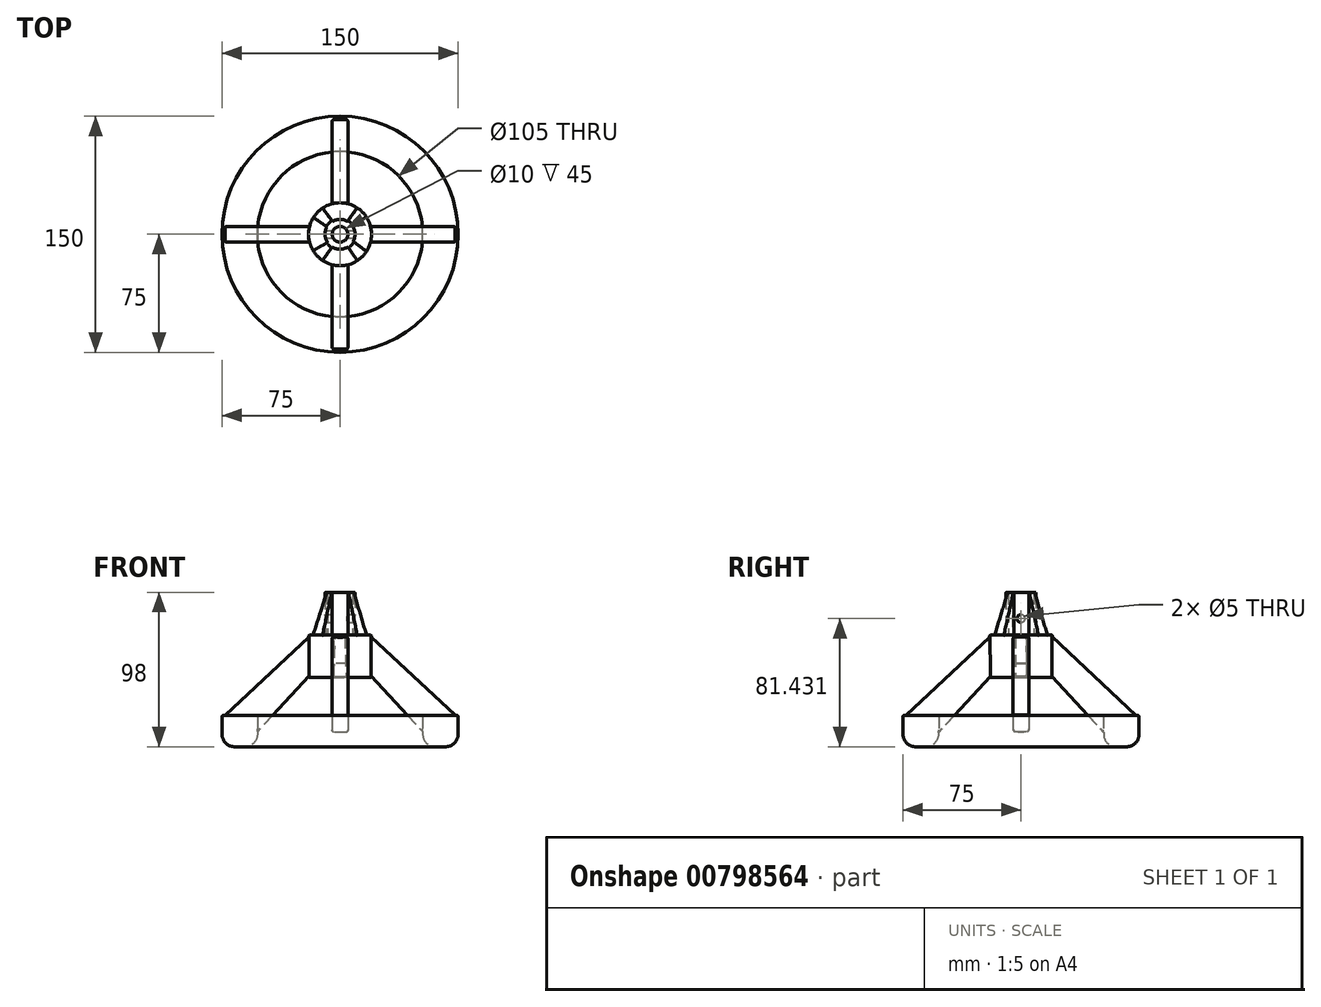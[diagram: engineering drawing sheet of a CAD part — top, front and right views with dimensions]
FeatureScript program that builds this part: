
annotation { "Feature Type Name" : "Feature", "Feature Type Description" : "" }
export const myFeature = defineFeature(function(context is Context, id is Id, definition is map)
    precondition{}
    {
        {
            var Q0;
            Q0=qCreatedBy(makeId("Top.planeOp"),FACE);
            var sketch = newSketch(context, id + "F0", { "sketchPlane" : qUnion([Q0])});
            skCircle(sketch, "E0", {"center": v(0, 0) * mm, "radius": 75 * mm});
            skCircle(sketch, "E1", {"center": v(0, 0) * mm, "radius": 52.5 * mm});
            skSolve(sketch);
        }
        {
            var Q0;
            Q0=makeQuery(id+"F0.imprint","IMPRINT",FACE,{"disambiguationData":[TD([[makeQuery(id+"F0.imprint","IMPRINT",EDGE,{"derivedFrom":sQuery(id+"F0.wireOp",EDGE,"E0")}),1.0]])]});
            extrude(context, id + "F1", {"entities" : qUnion([Q0]), "depth" : 20 * mm, "offsetDistance" : 25 * mm});
        }
        {
            var Q0;
            Q0=qCreatedBy(makeId("Top.planeOp"),FACE);
            var sketch = newSketch(context, id + "F2", { "sketchPlane" : qUnion([Q0])});
            skCircle(sketch, "E2", {"center": v(0, 0) * mm, "radius": 20 * mm});
            skSolve(sketch);
        }
        {
            var Q0;
            Q0=makeQuery(id+"F2.imprint","IMPRINT",FACE,{"disambiguationData":[TD([[makeQuery(id+"F2.imprint","IMPRINT",EDGE,{"derivedFrom":sQuery(id+"F2.wireOp",EDGE,"E2")}),1.0]])]});
            extrude(context, id + "F3", {"entities" : qUnion([Q0]), "operationType" : NewBodyOperationType.ADD, "depth" : 71 * mm, "offsetDistance" : 25 * mm, "hasSecondDirection" : true, "secondDirectionOppositeDirection" : false, "secondDirectionDepth" : 44 * mm});
        }
        {
            var Q0;
            Q0=makeQuery(id+"F3.opExtrude","CAP_FACE",FACE,{"disambiguationData":[OSD([sQuery(id+"F2.wireOp",EDGE,"E2")])],"isStart":false});
            var sketch = newSketch(context, id + "F4", { "sketchPlane" : qUnion([Q0])});
            skCircle(sketch, "E3", {"center": v(0, 0) * mm, "radius": 9.5 * mm});
            skLineSegment(sketch, "E4", {"start": v(4.72, 8.24) * mm, "end": v(10.9, 16.77) * mm});
            skLineSegment(sketch, "E5", {"start": v(8.08, 5) * mm, "end": v(16.66, 11.07) * mm});
            skLineSegment(sketch, "E6", {"start": v(-7.94, -5.21) * mm, "end": v(-17.13, -10.32) * mm});
            skLineSegment(sketch, "E7", {"start": v(-5.07, -8.04) * mm, "end": v(-11.07, -16.66) * mm});
            skLineSegment(sketch, "E8", {"start": v(-4.83, 8.18) * mm, "end": v(-11.08, 16.65) * mm});
            skLineSegment(sketch, "E9", {"start": v(-8.25, 4.7) * mm, "end": v(-16.9, 10.7) * mm});
            skLineSegment(sketch, "E10", {"start": v(8.35, -4.54) * mm, "end": v(16.78, -10.88) * mm});
            skLineSegment(sketch, "E11", {"start": v(5.1, -8.01) * mm, "end": v(10.88, -16.78) * mm});
            skSolve(sketch);
        }
        {
            var Q0;
            Q0=makeQuery(id+"F4.imprint","IMPRINT",FACE,{"disambiguationData":[TD([[makeQuery(id+"F4.imprint","IMPRINT",EDGE,{"derivedFrom":sQuery(id+"F4.wireOp",EDGE,"E3")}),1.0]])]});
            var Q1;
            {var subQ0=sQuery(id+"F4.wireOp",EDGE,"E6");Q1=makeQuery(id+"F4.imprint","IMPRINT",FACE,{"disambiguationData":[TD([[makeQuery(id+"F4.imprint","IMPRINT",EDGE,{"derivedFrom":subQ0}),1.0]])]});}
            var Q2;
            {var subQ0=sQuery(id+"F4.wireOp",EDGE,"E8");Q2=makeQuery(id+"F4.imprint","IMPRINT",FACE,{"disambiguationData":[TD([[makeQuery(id+"F4.imprint","IMPRINT",EDGE,{"derivedFrom":subQ0}),1.0]])]});}
            var Q3;
            {var subQ0=sQuery(id+"F4.wireOp",EDGE,"E4");Q3=makeQuery(id+"F4.imprint","IMPRINT",FACE,{"disambiguationData":[TD([[makeQuery(id+"F4.imprint","IMPRINT",EDGE,{"derivedFrom":subQ0}),-1.0]])]});}
            var Q4;
            {var subQ0=sQuery(id+"F4.wireOp",EDGE,"E10");Q4=makeQuery(id+"F4.imprint","IMPRINT",FACE,{"disambiguationData":[TD([[makeQuery(id+"F4.imprint","IMPRINT",EDGE,{"derivedFrom":subQ0}),-1.0]])]});}
            extrude(context, id + "F5", {"entities" : qUnion([Q0, Q1, Q2, Q3, Q4]), "operationType" : NewBodyOperationType.ADD, "depth" : 27 * mm, "offsetDistance" : 25 * mm});
        }
        {
            var Q0;
            Q0=qCreatedBy(makeId("Right.planeOp"),FACE);
            var sketch = newSketch(context, id + "F6", { "sketchPlane" : qUnion([Q0])});
            skPoint(sketch, "E12", {"position": v(0, 81.43) * mm});
            skSolve(sketch);
        }
        {
            var Q0;
            Q0=sQuery(id+"F6.wireOp",VERTEX,"E12");
            var Q1;
            Q1=makeQuery(id+"F3.opExtrude","SWEPT_BODY",BODY,{"disambiguationData":[OSD([sQuery(id+"F2.wireOp",EDGE,"E2")])]});
            hole(context, id + "F7", {"style" : HoleStyle.SIMPLE, "endStyle" : HoleEndStyle.THROUGH, "holeDiameter" : 5 * mm, "majorDiameter" : 5 * mm, "isTappedThrough" : true, "tappedDepth" : 12 * mm, "tapClearance" : 3, "locations" : qUnion([Q0]), "scope" : qUnion([Q1])});
        }
        {
            var Q0;
            Q0=sQuery(id+"F6.wireOp",VERTEX,"E12");
            var Q1;
            Q1=makeQuery(id+"F3.opExtrude","SWEPT_BODY",BODY,{"disambiguationData":[OSD([sQuery(id+"F2.wireOp",EDGE,"E2")])]});
            hole(context, id + "F8", {"style" : HoleStyle.SIMPLE, "endStyle" : HoleEndStyle.THROUGH, "oppositeDirection" : true, "holeDiameter" : 5 * mm, "majorDiameter" : 5 * mm, "isTappedThrough" : true, "tappedDepth" : 12 * mm, "tapClearance" : 3, "locations" : qUnion([Q0]), "scope" : qUnion([Q1])});
        }
        {
            var Q0;
            Q0=makeQuery(id+"F5.opExtrude","CAP_FACE",FACE,{"disambiguationData":[OSD([sQuery(id+"F4.wireOp",EDGE,"E3")])],"isStart":false});
            var sketch = newSketch(context, id + "F9", { "sketchPlane" : qUnion([Q0])});
            skCircle(sketch, "E13", {"center": v(0, 0) * mm, "radius": 5 * mm});
            skSolve(sketch);
        }
        {
            var Q0;
            Q0=makeQuery(id+"F9.imprint","IMPRINT",FACE,{"disambiguationData":[TD([[makeQuery(id+"F9.imprint","IMPRINT",EDGE,{"derivedFrom":sQuery(id+"F9.wireOp",EDGE,"E13")}),1.0]])]});
            extrude(context, id + "F10", {"entities" : qUnion([Q0]), "operationType" : NewBodyOperationType.REMOVE, "oppositeDirection" : true, "depth" : 45 * mm, "offsetDistance" : 25 * mm});
        }
        {
            var Q0;
            Q0=makeQuery(id+"F1.opExtrude","CAP_FACE",FACE,{"disambiguationData":[OSD([sQuery(id+"F0.wireOp",EDGE,"E0"),sQuery(id+"F0.wireOp",EDGE,"E1")])],"isStart":true});
            fillet(context, id + "F11", {"entities" : qUnion([Q0]), "radius" : 8 * mm, "tangentPropagation" : true, "allowEdgeOverflow" : false});
        }
        {
            var Q0;
            Q0=makeQuery(id+"F1.opExtrude","CAP_FACE",FACE,{"disambiguationData":[OSD([sQuery(id+"F0.wireOp",EDGE,"E0"),sQuery(id+"F0.wireOp",EDGE,"E1")])],"isStart":false});
            fillet(context, id + "F12", {"entities" : qUnion([Q0]), "radius" : 1 * mm, "tangentPropagation" : true, "allowEdgeOverflow" : false});
        }
        {
            var Q0;
            Q0=makeQuery(id+"F3.opExtrude","CAP_FACE",FACE,{"disambiguationData":[OSD([sQuery(id+"F2.wireOp",EDGE,"E2")])],"isStart":true});
            fillet(context, id + "F13", {"entities" : qUnion([Q0]), "radius" : 1 * mm, "tangentPropagation" : true, "allowEdgeOverflow" : false});
        }
        {
            var Q0;
            Q0=makeQuery(id+"F3.opExtrude","CAP_EDGE",EDGE,{"disambiguationData":[OSD([sQuery(id+"F2.wireOp",EDGE,"E2")])],"isStart":false});
            fillet(context, id + "F14", {"entities" : qUnion([Q0]), "radius" : 1 * mm, "tangentPropagation" : true, "allowEdgeOverflow" : false});
        }
        {
            var Q0;
            Q0=qCreatedBy(makeId("Front.planeOp"),FACE);
            var sketch = newSketch(context, id + "F15", { "sketchPlane" : qUnion([Q0])});
            skLineSegment(sketch, "E14", {"start": v(-74.56, 18.72) * mm, "end": v(-19.69, 69.8) * mm});
            skLineSegment(sketch, "E15", {"start": v(-19.69, 69.8) * mm, "end": v(-19.69, 44.9) * mm});
            skLineSegment(sketch, "E16", {"start": v(-19.69, 44.9) * mm, "end": v(-61.49, 0) * mm});
            skLineSegment(sketch, "E17", {"start": v(-74.56, 18.72) * mm, "end": v(-73.96, 6.47) * mm});
            skLineSegment(sketch, "E18", {"start": v(-73.96, 6.47) * mm, "end": v(-71.63, 2.64) * mm});
            skLineSegment(sketch, "E19", {"start": v(-71.63, 2.64) * mm, "end": v(-68.78, 1.1) * mm});
            skLineSegment(sketch, "E20", {"start": v(-68.78, 1.1) * mm, "end": v(-61.49, 0) * mm});
            skLineSegment(sketch, "E21", {"start": v(19.64, 44.85) * mm, "end": v(61.35, 0) * mm});
            skLineSegment(sketch, "E22", {"start": v(61.35, 0) * mm, "end": v(69.64, 1.41) * mm});
            skLineSegment(sketch, "E23", {"start": v(69.64, 1.41) * mm, "end": v(72.9, 4.92) * mm});
            skLineSegment(sketch, "E24", {"start": v(72.9, 4.92) * mm, "end": v(72.9, 20.35) * mm});
            skLineSegment(sketch, "E25", {"start": v(72.9, 20.35) * mm, "end": v(19.7, 69.87) * mm});
            skLineSegment(sketch, "E26", {"start": v(19.7, 69.87) * mm, "end": v(19.64, 44.85) * mm});
            skSolve(sketch);
        }
        {
            var Q0;
            Q0 = qSketchRegion(id + "F15", true);
            extrude(context, id + "F16", {"entities" : qUnion([Q0]), "operationType" : NewBodyOperationType.ADD, "depth" : 5 * mm, "offsetDistance" : 25 * mm, "hasSecondDirection" : true, "secondDirectionOppositeDirection" : true, "secondDirectionDepth" : 5 * mm});
        }
        {
            var Q0;
            Q0=qCreatedBy(makeId("Right.planeOp"),FACE);
            var sketch = newSketch(context, id + "F17", { "sketchPlane" : qUnion([Q0])});
            skLineSegment(sketch, "E27", {"start": v(19.63, 44.78) * mm, "end": v(60.8, 0) * mm});
            skLineSegment(sketch, "E28", {"start": v(60.8, 0) * mm, "end": v(66.69, 0) * mm});
            skLineSegment(sketch, "E29", {"start": v(66.69, 0) * mm, "end": v(70.81, 1.85) * mm});
            skLineSegment(sketch, "E30", {"start": v(70.81, 1.85) * mm, "end": v(73.14, 4.43) * mm});
            skLineSegment(sketch, "E31", {"start": v(73.14, 4.43) * mm, "end": v(74.42, 7.52) * mm});
            skLineSegment(sketch, "E32", {"start": v(74.42, 7.52) * mm, "end": v(74.42, 18.6) * mm});
            skLineSegment(sketch, "E33", {"start": v(74.42, 18.6) * mm, "end": v(19.76, 69.92) * mm});
            skLineSegment(sketch, "E34", {"start": v(19.76, 69.92) * mm, "end": v(19.63, 44.78) * mm});
            skLineSegment(sketch, "E35", {"start": v(-19.3, 44.65) * mm, "end": v(-60.88, 0) * mm});
            skLineSegment(sketch, "E36", {"start": v(-60.88, 0) * mm, "end": v(-66.16, 0) * mm});
            skLineSegment(sketch, "E37", {"start": v(-66.16, 0) * mm, "end": v(-70.36, 1.46) * mm});
            skLineSegment(sketch, "E38", {"start": v(-70.36, 1.46) * mm, "end": v(-73.2, 4.17) * mm});
            skLineSegment(sketch, "E39", {"start": v(-73.2, 4.17) * mm, "end": v(-74.23, 7.78) * mm});
            skLineSegment(sketch, "E40", {"start": v(-74.23, 7.78) * mm, "end": v(-74.23, 18.86) * mm});
            skLineSegment(sketch, "E41", {"start": v(-74.23, 18.86) * mm, "end": v(-19.7, 69.8) * mm});
            skLineSegment(sketch, "E42", {"start": v(-19.7, 69.8) * mm, "end": v(-19.3, 44.65) * mm});
            skSolve(sketch);
        }
        {
            var Q0;
            Q0 = qSketchRegion(id + "F17", true);
            extrude(context, id + "F18", {"entities" : qUnion([Q0]), "operationType" : NewBodyOperationType.ADD, "depth" : 5 * mm, "offsetDistance" : 25 * mm, "hasSecondDirection" : true, "secondDirectionOppositeDirection" : true, "secondDirectionDepth" : 5 * mm});
        }
        {
            var Q0;
            Q0=makeQuery(id+"F16.opExtrude","CAP_EDGE",EDGE,{"disambiguationData":[OSD([sQuery(id+"F15.wireOp",EDGE,"E21")])],"isStart":true});
            var Q1;
            Q1=makeQuery(id+"F16.opExtrude","CAP_EDGE",EDGE,{"disambiguationData":[OSD([sQuery(id+"F15.wireOp",EDGE,"E21")])],"isStart":false});
            var Q2;
            Q2=makeQuery(id+"F18.opExtrude","CAP_EDGE",EDGE,{"disambiguationData":[OSD([sQuery(id+"F17.wireOp",EDGE,"E27")])],"isStart":true});
            var Q3;
            Q3=makeQuery(id+"F18.opExtrude","CAP_EDGE",EDGE,{"disambiguationData":[OSD([sQuery(id+"F17.wireOp",EDGE,"E27")])],"isStart":false});
            var Q4;
            Q4=makeQuery(id+"F16.opExtrude","CAP_EDGE",EDGE,{"disambiguationData":[OSD([sQuery(id+"F15.wireOp",EDGE,"E16")])],"isStart":true});
            var Q5;
            Q5=makeQuery(id+"F16.opExtrude","CAP_EDGE",EDGE,{"disambiguationData":[OSD([sQuery(id+"F15.wireOp",EDGE,"E16")])],"isStart":false});
            var Q6;
            Q6=makeQuery(id+"F18.opExtrude","CAP_EDGE",EDGE,{"disambiguationData":[OSD([sQuery(id+"F17.wireOp",EDGE,"E35")])],"isStart":false});
            var Q7;
            Q7=makeQuery(id+"F18.opExtrude","CAP_EDGE",EDGE,{"disambiguationData":[OSD([sQuery(id+"F17.wireOp",EDGE,"E35")])],"isStart":true});
            fillet(context, id + "F19", {"entities" : qUnion([Q0, Q1, Q2, Q3, Q4, Q5, Q6, Q7]), "radius" : 1 * mm, "tangentPropagation" : true, "allowEdgeOverflow" : false});
        }
        {
            var Q0;
            Q0=makeQuery(id+"F18.opExtrude","CAP_EDGE",EDGE,{"disambiguationData":[OSD([sQuery(id+"F17.wireOp",EDGE,"E33")])],"isStart":false});
            var Q1;
            Q1=makeQuery(id+"F18.opExtrude","CAP_EDGE",EDGE,{"disambiguationData":[OSD([sQuery(id+"F17.wireOp",EDGE,"E33")])],"isStart":true});
            var Q2;
            Q2=makeQuery(id+"F16.opExtrude","CAP_EDGE",EDGE,{"disambiguationData":[OSD([sQuery(id+"F15.wireOp",EDGE,"E25")])],"isStart":false});
            var Q3;
            Q3=makeQuery(id+"F16.opExtrude","CAP_EDGE",EDGE,{"disambiguationData":[OSD([sQuery(id+"F15.wireOp",EDGE,"E25")])],"isStart":true});
            var Q4;
            Q4=makeQuery(id+"F18.opExtrude","CAP_EDGE",EDGE,{"disambiguationData":[OSD([sQuery(id+"F17.wireOp",EDGE,"E41")])],"isStart":false});
            var Q5;
            Q5=makeQuery(id+"F18.opExtrude","CAP_EDGE",EDGE,{"disambiguationData":[OSD([sQuery(id+"F17.wireOp",EDGE,"E41")])],"isStart":true});
            var Q6;
            Q6=makeQuery(id+"F16.opExtrude","CAP_EDGE",EDGE,{"disambiguationData":[OSD([sQuery(id+"F15.wireOp",EDGE,"E14")])],"isStart":true});
            var Q7;
            Q7=makeQuery(id+"F16.opExtrude","CAP_EDGE",EDGE,{"disambiguationData":[OSD([sQuery(id+"F15.wireOp",EDGE,"E14")])],"isStart":false});
            fillet(context, id + "F20", {"entities" : qUnion([Q0, Q1, Q2, Q3, Q4, Q5, Q6, Q7]), "radius" : 1 * mm, "tangentPropagation" : true, "allowEdgeOverflow" : false});
        }
        {
            var Q0;
            {var subQ0=sQuery(id+"F2.wireOp",EDGE,"E2");var subQ1=makeQuery(id+"F3.opExtrude","CAP_EDGE",EDGE,{"disambiguationData":[OSD([subQ0])],"isStart":false});Q0=makeQuery(id+"F5.opExtrude","CAP_EDGE",EDGE,{"disambiguationData":[OSD([subQ0]),TDD([makeQuery(id+"F4.imprint","IMPRINT",EDGE,{"disambiguationData":[TD([[makeQuery(id+"F4.imprint","INTERSECT",VERTEX,{"derivedFrom":[subQ1,sQuery(id+"F4.wireOp",EDGE,"E6")]}),-1.0]])],"derivedFrom":subQ1})])],"isStart":false});}
            var Q1;
            {var subQ0=sQuery(id+"F2.wireOp",EDGE,"E2");var subQ1=makeQuery(id+"F3.opExtrude","CAP_EDGE",EDGE,{"disambiguationData":[OSD([subQ0])],"isStart":false});Q1=makeQuery(id+"F5.opExtrude","CAP_EDGE",EDGE,{"disambiguationData":[OSD([subQ0]),TDD([makeQuery(id+"F4.imprint","IMPRINT",EDGE,{"disambiguationData":[TD([[makeQuery(id+"F4.imprint","INTERSECT",VERTEX,{"derivedFrom":[subQ1,sQuery(id+"F4.wireOp",EDGE,"E8")]}),-1.0]])],"derivedFrom":subQ1})])],"isStart":false});}
            var Q2;
            {var subQ0=sQuery(id+"F2.wireOp",EDGE,"E2");var subQ1=makeQuery(id+"F3.opExtrude","CAP_EDGE",EDGE,{"disambiguationData":[OSD([subQ0])],"isStart":false});Q2=makeQuery(id+"F5.opExtrude","CAP_EDGE",EDGE,{"disambiguationData":[OSD([subQ0]),TDD([makeQuery(id+"F4.imprint","IMPRINT",EDGE,{"disambiguationData":[TD([[makeQuery(id+"F4.imprint","INTERSECT",VERTEX,{"derivedFrom":[subQ1,sQuery(id+"F4.wireOp",EDGE,"E4")]}),1.0]])],"derivedFrom":subQ1})])],"isStart":false});}
            var Q3;
            {var subQ0=sQuery(id+"F2.wireOp",EDGE,"E2");var subQ1=makeQuery(id+"F3.opExtrude","CAP_EDGE",EDGE,{"disambiguationData":[OSD([subQ0])],"isStart":false});Q3=makeQuery(id+"F5.opExtrude","CAP_EDGE",EDGE,{"disambiguationData":[OSD([subQ0]),TDD([makeQuery(id+"F4.imprint","IMPRINT",EDGE,{"disambiguationData":[TD([[makeQuery(id+"F4.imprint","INTERSECT",VERTEX,{"derivedFrom":[subQ1,sQuery(id+"F4.wireOp",EDGE,"E10")]}),1.0]])],"derivedFrom":subQ1})])],"isStart":false});}
            chamfer(context, id + "F21", {"entities" : qUnion([Q0, Q1, Q2, Q3]), "chamferType" : ChamferType.TWO_OFFSETS, "width1" : 10 * mm, "oppositeDirection" : false, "width2" : 27 * mm, "tangentPropagation" : true});
        }
    });
